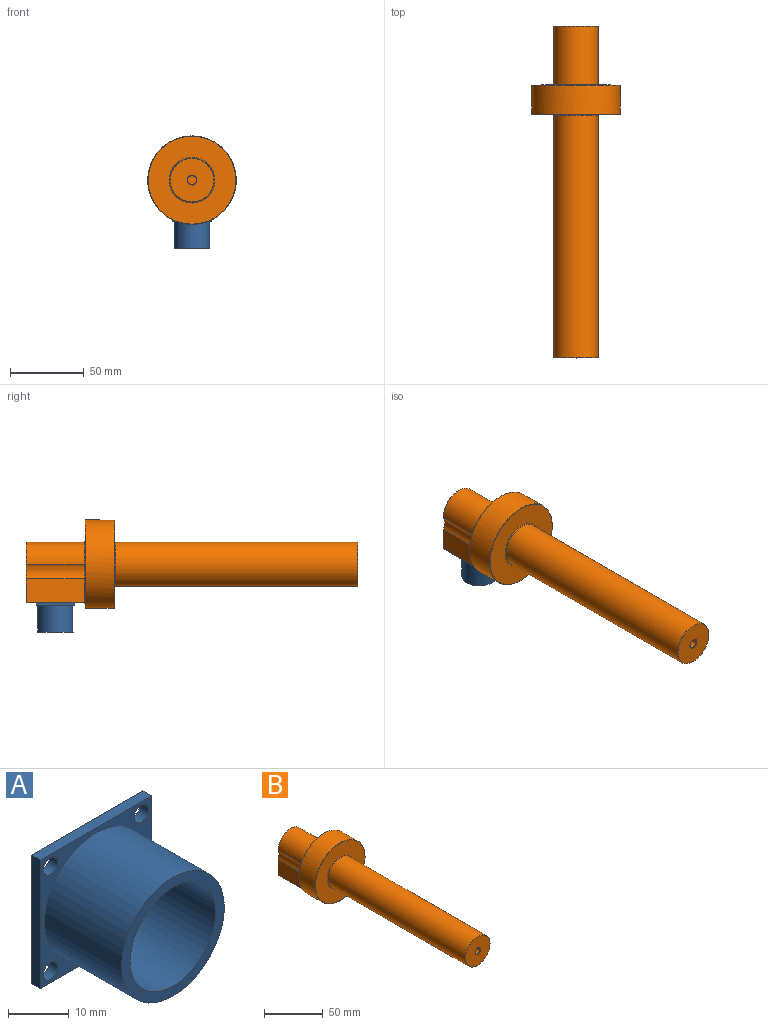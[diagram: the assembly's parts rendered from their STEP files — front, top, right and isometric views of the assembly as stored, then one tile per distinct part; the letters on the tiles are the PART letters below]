
ASSEMBLY  parts=2 mates=1
PART A: 14 faces, bbox 26x20x26 mm
  f0: cylinder r=10mm len=20mm, axis (0,1,0), area 1131mm2, adj f2,f3
  f1: cylinder r=12mm len=24mm, axis (0,1,0), area 1357.2mm2, adj f2,f12
  f2: plane 24x24mm, normal (0,-1,0), area 138.2mm2, adj f0,f1
  f3: plane 20x20mm, normal (0,-1,0), area 314.2mm2, adj f0
  f4: plane 26x2mm, normal (0,0,-1), area 52mm2, adj f5,f11,f12,f13
  f5: plane 26x2mm, normal (1,0,0), area 52mm2, adj f4,f6,f12,f13
  f6: plane 26x2mm, normal (0,0,1), area 52mm2, adj f5,f11,f12,f13
  f7: cylinder r=1.7mm len=3.4mm, axis (0,-1,0), area 21.4mm2, adj f12,f13
  f8: cylinder r=1.7mm len=3.4mm, axis (0,-1,0), area 21.4mm2, adj f12,f13
  f9: cylinder r=1.7mm len=3.4mm, axis (0,-1,0), area 21.4mm2, adj f12,f13
  f10: cylinder r=1.7mm len=3.4mm, axis (0,-1,0), area 21.4mm2, adj f12,f13
  f11: plane 26x2mm, normal (-1,0,0), area 52mm2, adj f4,f6,f12,f13
  f12: plane 26x26mm, normal (0,-1,0), area 187.3mm2, adj f1,f4,f5,f6,f7,f8,f9,f10
  f13: plane 26x26mm, normal (0,1,0), area 639.7mm2, adj f4,f5,f6,f7,f8,f9,f10,f11
PART B: 51 faces, bbox 60x225x60 mm
  f0: cone r=0mm half-angle=59deg, axis (0,0,-1), area 9.4mm2, adj f1
  f1: cylinder r=1.6mm len=10mm, axis (0,0,-1), area 100.5mm2, adj f0,f12
  f2: cone r=0mm half-angle=59deg, axis (0,0,-1), area 9.4mm2, adj f3
  f3: cylinder r=1.6mm len=10mm, axis (0,0,-1), area 100.5mm2, adj f2,f12
  f4: cone r=0mm half-angle=59deg, axis (0,0,-1), area 9.4mm2, adj f5
  f5: cylinder r=1.6mm len=10mm, axis (0,0,-1), area 100.5mm2, adj f4,f12
  f6: cone r=30mm half-angle=45deg, axis (0,-1,0), area 66.8mm2, adj f8,f12,f13,f15,f16,f19,f32,f40
  f7: cylinder r=10mm len=219.75mm, axis (0,1,0), area 13407.3mm2, adj f20,f21,f41
  f8: cylinder r=30mm len=60mm, axis (0,-1,0), area 3675.7mm2, adj f6,f27
  f9: plane 40.48x29.5mm, normal (0,1,0), area 752.4mm2, adj f31,f33,f34,f36,f37,f38,f41
  f10: cylinder r=15mm len=164.25mm, axis (0,1,0), area 15480.2mm2, adj f29,f42
  f11: plane 59.5x59.5mm, normal (0,-1,0), area 2025.7mm2, adj f27,f42
  f12: plane 39.9x29.52mm, normal (0,0,-1), area 796.5mm2, adj f1,f3,f5,f6,f30,f32,f37,f40
  f13: plane 27.12x3.27mm, normal (0,1,0), area 59.8mm2, adj f6,f43
  f14: cylinder r=10mm len=39.25mm, axis (0,1,0), area 411mm2, adj f15,f18,f36,f45
  f15: plane 39.79x15.73mm, normal (-1,0,0), area 617.6mm2, adj f6,f14,f38,f40,f44
  f16: plane 39.79x15.73mm, normal (1,0,0), area 617.6mm2, adj f6,f17,f32,f33,f47
  f17: cylinder r=10mm len=39.25mm, axis (0,1,0), area 411mm2, adj f16,f18,f31,f48
  f18: cylinder r=15mm len=39.25mm, axis (0,1,0), area 1849.6mm2, adj f14,f17,f34,f46
  f19: plane 59.5x55.14mm, normal (0,1,0), area 1542.1mm2, adj f6,f44,f45,f46,f47,f48
  f20: cylinder r=10mm len=25.73mm, axis (0,0,-1), area 1216.7mm2, adj f7,f30
  f21: plane 20x20mm, normal (0,1,0), area 263.9mm2, adj f7,f25
  f22: cylinder r=3mm len=6mm, axis (0,1,0), area 89.5mm2, adj f24,f28
  f23: plane 29.5x29.5mm, normal (0,-1,0), area 650.3mm2, adj f28,f29
  f24: plane 6x6mm, normal (0,-1,0), area 28.3mm2, adj f22
  f25: cylinder r=4mm len=160mm, axis (0,1,0), area 4021.2mm2, adj f21,f26
  f26: plane 8x8mm, normal (0,1,0), area 50.3mm2, adj f25
  f27: cone r=29.75mm half-angle=45deg, axis (0,1,0), area 66.4mm2, adj f8,f11
  f28: cone r=3mm half-angle=45deg, axis (0,-1,0), area 6.9mm2, adj f22,f23
  f29: cone r=14.75mm half-angle=45deg, axis (0,1,0), area 33mm2, adj f10,f23
  f30: cone r=10mm half-angle=45deg, axis (0,0,-1), area 22.5mm2, adj f12,f20
  f31: cone r=10.25mm half-angle=45deg, axis (0,1,0), area 3.7mm2, adj f9,f17,f33,f34
  f32: plane 39.88x0.25mm, normal (0.71,0,-0.71), area 14.1mm2, adj f6,f12,f16,f35
  f33: plane 15.73x0.25mm, normal (0.71,0.71,0), area 5.5mm2, adj f9,f16,f31,f35
  f34: cone r=15mm half-angle=45deg, axis (0,-1,0), area 16.5mm2, adj f9,f18,f31,f36
  f35: plane 0.25x0.25mm, normal (0.58,0.58,-0.58), area 0.1mm2, adj f32,f33,f37
  f36: cone r=10mm half-angle=45deg, axis (0,1,0), area 3.7mm2, adj f9,f14,f34,f38
  f37: plane 29.5x0.25mm, normal (0,0.71,-0.71), area 10.4mm2, adj f9,f12,f35,f39
  f38: plane 15.73x0.25mm, normal (-0.71,0.71,0), area 5.5mm2, adj f9,f15,f36,f39
  f39: plane 0.25x0.25mm, normal (-0.58,0.58,-0.58), area 0.1mm2, adj f37,f38,f40
  f40: plane 39.88x0.25mm, normal (-0.71,0,-0.71), area 14.1mm2, adj f6,f12,f15,f39
  f41: cone r=10.25mm half-angle=45deg, axis (0,1,0), area 22.5mm2, adj f7,f9
  f42: torus R=15.5mm, axis (0,-1,0), area 74.9mm2, adj f10,f11
  f43: cylinder r=0.5mm len=27.84mm, axis (1,0,0), area 21.6mm2, adj f6,f12,f13
  f44: cylinder r=0.5mm len=15.6mm, axis (0,0,-1), area 12.1mm2, adj f6,f15,f19,f45
  f45: torus R=9.5mm, axis (0,1,0), area 8.2mm2, adj f14,f19,f44,f46
  f46: torus R=15.5mm, axis (0,1,0), area 37.6mm2, adj f18,f19,f45,f48
  f47: cylinder r=0.5mm len=15.6mm, axis (0,0,1), area 12.1mm2, adj f6,f16,f19,f48
  f48: torus R=9.5mm, axis (0,1,0), area 8.2mm2, adj f17,f19,f46,f47
  f49: cone r=0mm half-angle=59deg, axis (0,0,-1), area 9.4mm2, adj f50
  f50: cylinder r=1.6mm len=10mm, axis (0,0,-1), area 100.5mm2, adj f12,f49
PLACE A rot(axis=(1,0,0),90deg) t=(55.97,35.74,-46.49)mm
PLACE B t=(55.97,-4.23,-18.51)mm
MATE fastened B.f0 <-> A.f10  axis (0,0,-1) through (66.58,46.34,-44.49)mm
